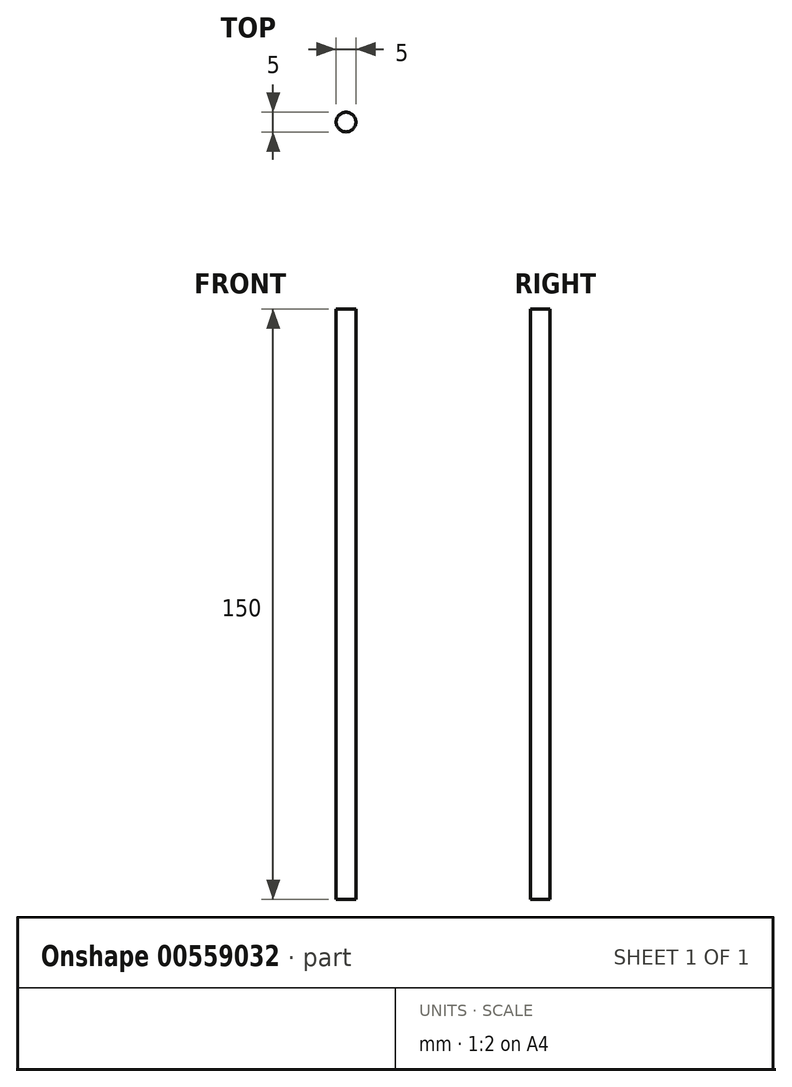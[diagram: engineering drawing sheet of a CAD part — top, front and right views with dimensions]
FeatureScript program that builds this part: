
annotation { "Feature Type Name" : "Feature", "Feature Type Description" : "" }
export const myFeature = defineFeature(function(context is Context, id is Id, definition is map)
    precondition{}
    {
        {
            var Q0;
            Q0=qCreatedBy(makeId("Top.planeOp"),FACE);
            var sketch = newSketch(context, id + "F0", { "sketchPlane" : qUnion([Q0])});
            skCircle(sketch, "E0", {"center": v(0, 0) * mm, "radius": 2.5 * mm});
            skSolve(sketch);
        }
        {
            var Q0;
            Q0 = qSketchRegion(id + "F0", true);
            extrude(context, id + "F1", {"entities" : qUnion([Q0]), "depth" : 150 * mm, "offsetDistance" : 25 * mm});
        }
    });
